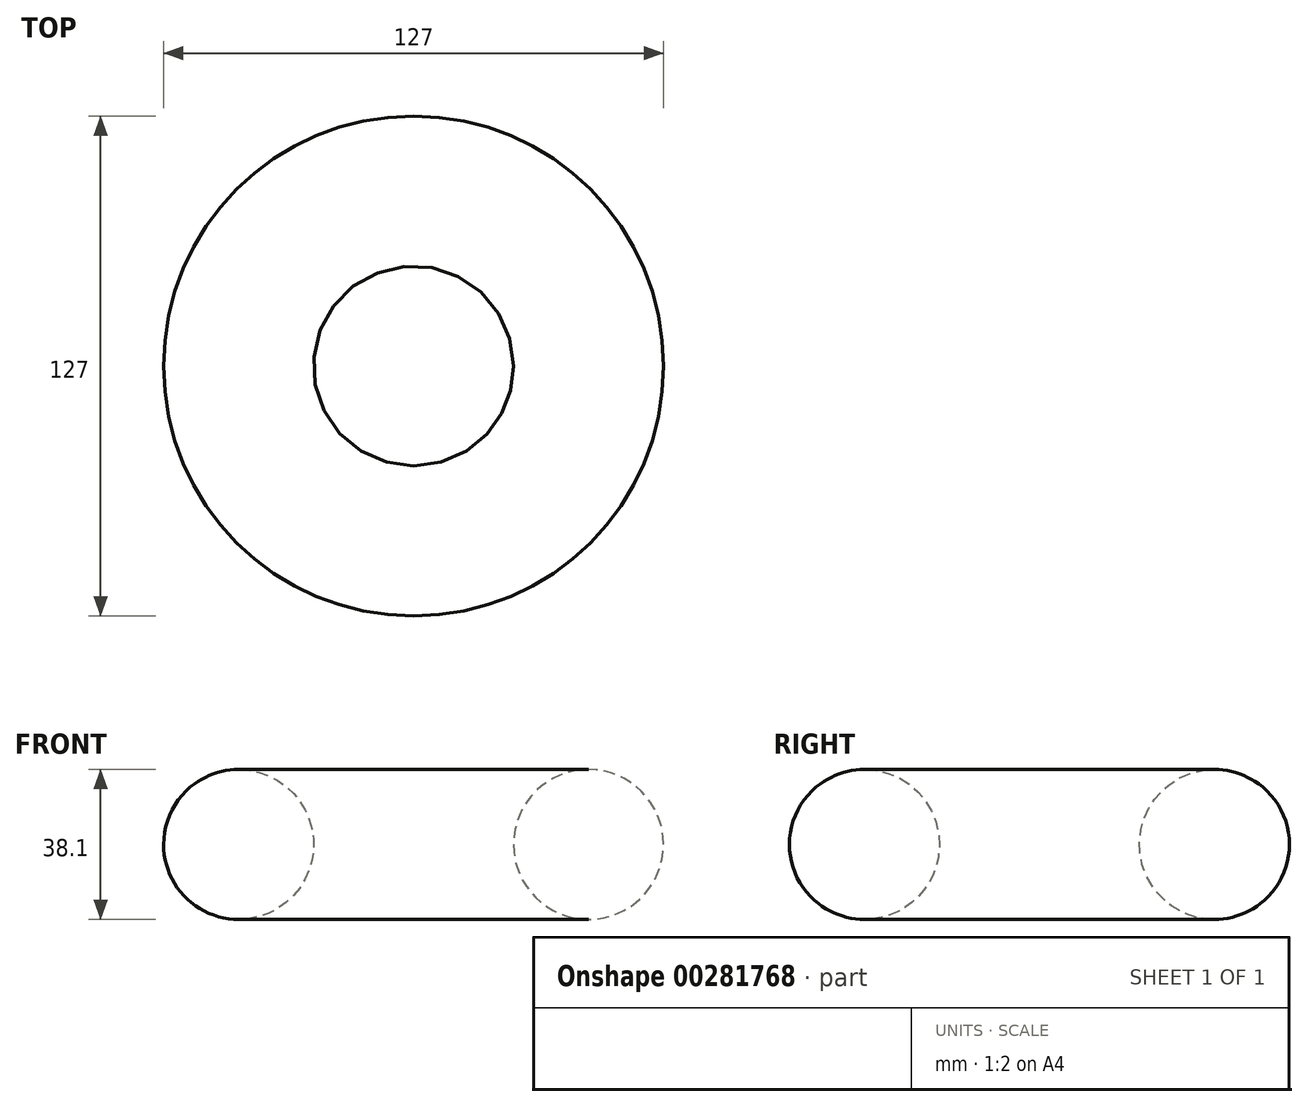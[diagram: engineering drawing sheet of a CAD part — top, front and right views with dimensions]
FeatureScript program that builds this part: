
annotation { "Feature Type Name" : "Feature", "Feature Type Description" : "" }
export const myFeature = defineFeature(function(context is Context, id is Id, definition is map)
    precondition{}
    {
        {
            var Q0;
            Q0=qCreatedBy(makeId("Front.planeOp"),FACE);
            var sketch = newSketch(context, id + "F0", { "sketchPlane" : qUnion([Q0])});
            skLineSegment(sketch, "E0", {"start": v(0, 51.37) * mm, "end": v(0, -41.18) * mm});
            skCircle(sketch, "E1", {"center": v(-44.45, 0) * mm, "radius": 19.05 * mm});
            skSolve(sketch);
        }
        {
            var Q0;
            Q0 = qSketchRegion(id + "F0", true);
            var Q1;
            Q1=sQuery(id+"F0.wireOp",EDGE,"E0");
            revolve(context, id + "F1", {"entities" : qUnion([Q0]), "axis" : qUnion([Q1]), "revolveType" : RevolveType.FULL});
        }
    });
